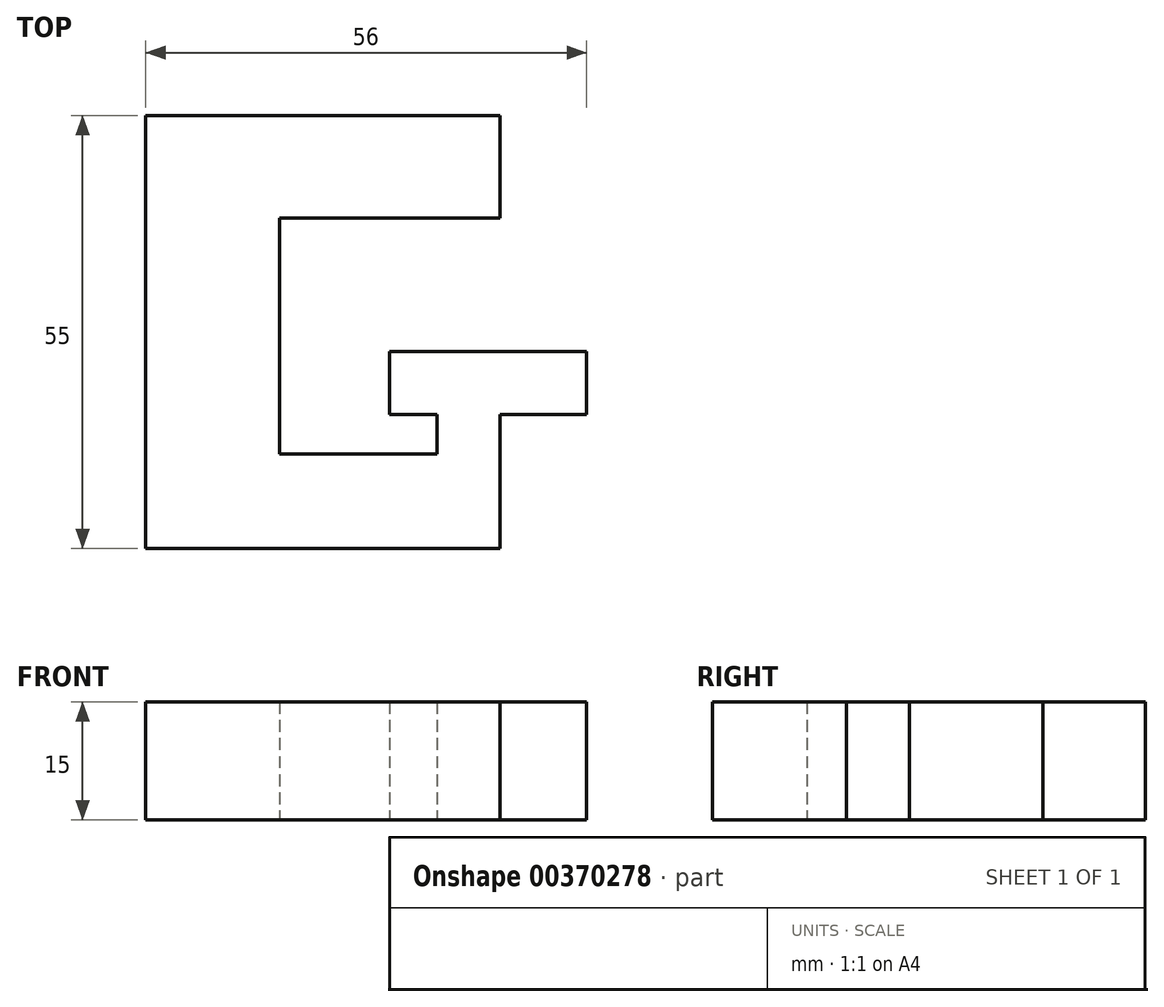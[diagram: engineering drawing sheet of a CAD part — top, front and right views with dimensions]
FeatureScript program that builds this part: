
annotation { "Feature Type Name" : "Feature", "Feature Type Description" : "" }
export const myFeature = defineFeature(function(context is Context, id is Id, definition is map)
    precondition{}
    {
        {
            var Q0;
            Q0=qCreatedBy(makeId("Top.planeOp"),FACE);
            var sketch = newSketch(context, id + "F0", { "sketchPlane" : qUnion([Q0])});
            skLineSegment(sketch, "E0", {"start": v(0, 0) * mm, "end": v(45, 0) * mm});
            skLineSegment(sketch, "E1", {"start": v(45, 0) * mm, "end": v(45, 17) * mm});
            skLineSegment(sketch, "E2", {"start": v(45, 17) * mm, "end": v(56, 17) * mm});
            skLineSegment(sketch, "E3", {"start": v(56, 17) * mm, "end": v(56, 25) * mm});
            skLineSegment(sketch, "E4", {"start": v(56, 25) * mm, "end": v(31, 25) * mm});
            skLineSegment(sketch, "E5", {"start": v(31, 25) * mm, "end": v(31, 17) * mm});
            skLineSegment(sketch, "E6", {"start": v(31, 17) * mm, "end": v(37, 17) * mm});
            skLineSegment(sketch, "E7", {"start": v(37, 17) * mm, "end": v(37, 12) * mm});
            skLineSegment(sketch, "E8", {"start": v(37, 12) * mm, "end": v(17, 12) * mm});
            skLineSegment(sketch, "E9", {"start": v(17, 12) * mm, "end": v(17, 42) * mm});
            skLineSegment(sketch, "E10", {"start": v(17, 42) * mm, "end": v(45, 42) * mm});
            skLineSegment(sketch, "E11", {"start": v(45, 42) * mm, "end": v(45, 55) * mm});
            skLineSegment(sketch, "E12", {"start": v(45, 55) * mm, "end": v(0, 55) * mm});
            skLineSegment(sketch, "E13", {"start": v(0, 55) * mm, "end": v(0, 0) * mm});
            skSolve(sketch);
        }
        {
            var Q0;
            Q0 = qSketchRegion(id + "F0", true);
            extrude(context, id + "F1", {"entities" : qUnion([Q0]), "depth" : 15 * mm});
        }
    });
